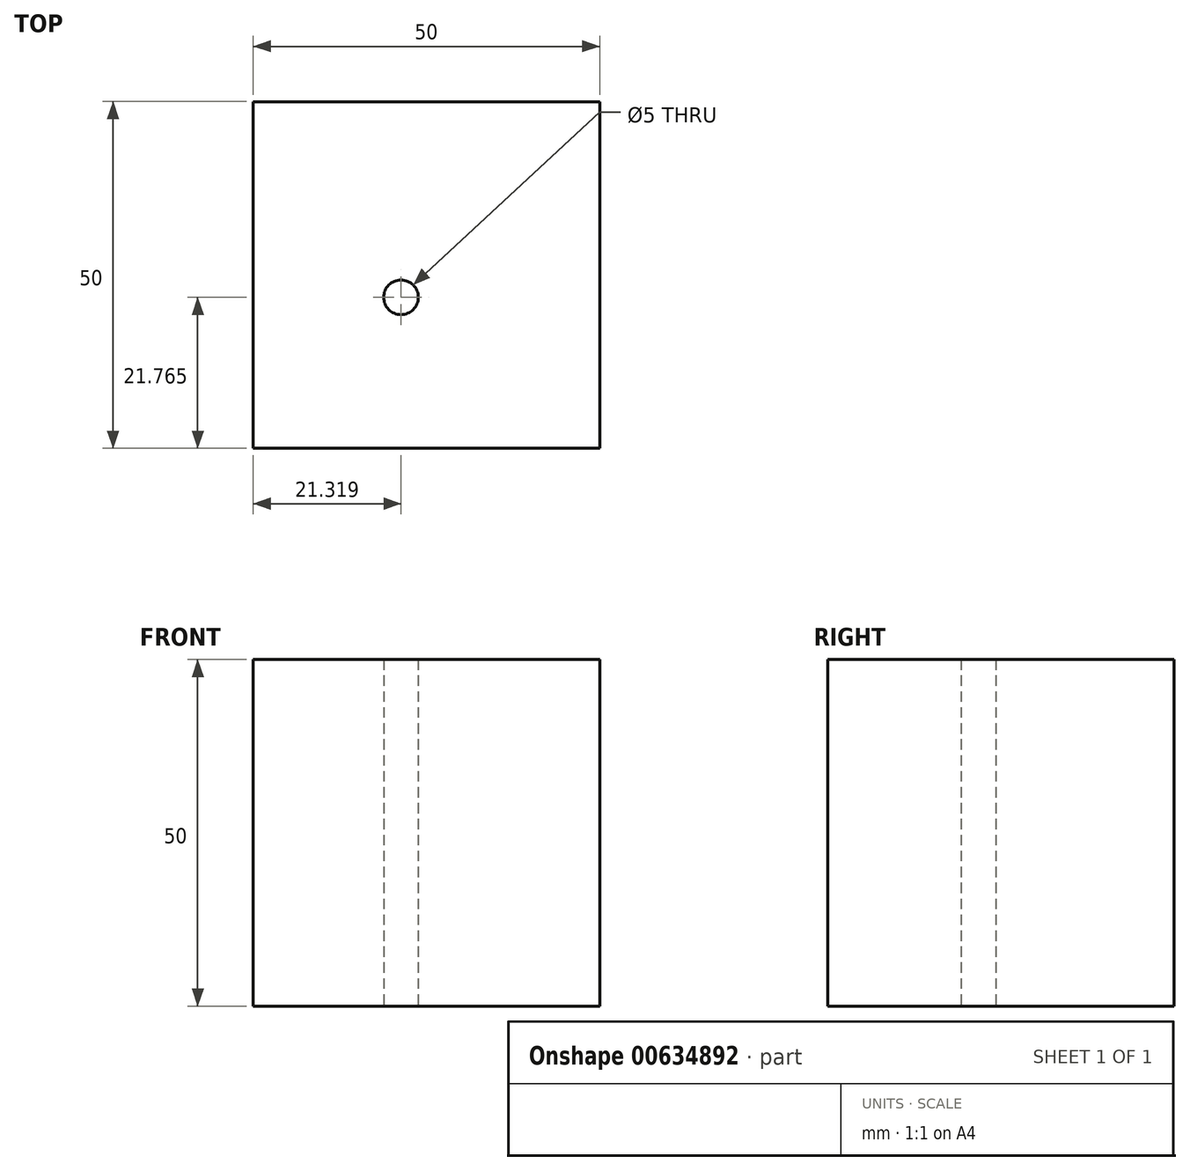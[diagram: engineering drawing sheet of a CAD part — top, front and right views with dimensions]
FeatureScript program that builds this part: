
annotation { "Feature Type Name" : "Feature", "Feature Type Description" : "" }
export const myFeature = defineFeature(function(context is Context, id is Id, definition is map)
    precondition{}
    {
        {
            var Q0;
            Q0=qCreatedBy(makeId("Top.planeOp"),FACE);
            var sketch = newSketch(context, id + "F0", { "sketchPlane" : qUnion([Q0])});
            skLineSegment(sketch, "E0.bottom", {"start": v(-659.4, -916.01) * mm, "end": v(-609.4, -916.01) * mm});
            skLineSegment(sketch, "E0.top", {"start": v(-659.4, -866.01) * mm, "end": v(-609.4, -866.01) * mm});
            skLineSegment(sketch, "E0.left", {"start": v(-659.4, -916.01) * mm, "end": v(-659.4, -866.01) * mm});
            skLineSegment(sketch, "E0.right", {"start": v(-609.4, -916.01) * mm, "end": v(-609.4, -866.01) * mm});
            skCircle(sketch, "E1", {"center": v(-638.08, -894.25) * mm, "radius": 2.5 * mm});
            skSolve(sketch);
        }
        {
            var Q0;
            Q0 = qSketchRegion(id + "F0", true);
            extrude(context, id + "F1", {"entities" : qUnion([Q0]), "depth" : 50 * mm, "offsetDistance" : 25 * mm});
        }
        {
            var Q0;
            Q0=sQuery(id+"F0.wireOp",VERTEX,"E1.center");
            var Q1;
            Q1=makeQuery(id+"F1.opExtrude","SWEPT_BODY",BODY,{"disambiguationData":[OSD([sQuery(id+"F0.wireOp",EDGE,"E0.bottom"),sQuery(id+"F0.wireOp",EDGE,"E0.top"),sQuery(id+"F0.wireOp",EDGE,"E0.left"),sQuery(id+"F0.wireOp",EDGE,"E0.right"),sQuery(id+"F0.wireOp",EDGE,"E1")])]});
            hole(context, id + "F2", {"style" : HoleStyle.SIMPLE, "endStyle" : HoleEndStyle.BLIND, "standardTappedOrClearance" : lookupTablePath({ "standard" : "ISO", "engagement" : "75%", "pitch" : "2.5 mm", "size" : "M20", "type" : "Tapped" }), "standardBlindInLast" : lookupTablePath({ "standard" : "ISO", "engagement" : "75%", "pitch" : "2.5 mm", "size" : "M20", "type" : "Tapped" }), "holeDiameter" : 17.5 * mm, "majorDiameter" : 20 * mm, "showTappedDepth" : true, "holeDepth" : 22.5 * mm, "isTappedThrough" : true, "tappedDepth" : 15 * mm, "tapClearance" : 3, "locations" : qUnion([Q0]), "scope" : qUnion([Q1])});
        }
    });
